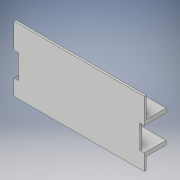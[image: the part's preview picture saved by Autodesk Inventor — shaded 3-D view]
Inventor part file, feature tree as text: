
AUTODESK INVENTOR PART (.ipt)
format: ipt  version: 2019 (Build 230136000, 136)  size: 131,584 bytes
history: native  units: in
note: dims shown in document units (in); Inventor stores cm internally (conversion verified against a paired STEP export)
features: sketch x4, extrude x3
ambient origin geometry x8: Origin, YZ Plane, XZ Plane, XY Plane, X Axis, Y Axis, Z Axis, Center Point
bodies: Solid1 (feature_tree)
feature tree (7):
  extrude  "Extrusion1"  Depth=9.8425in
  sketch  "Sketch2"  dims[d2=0.315in d3=0.0in d4=0.315in d5=0.0in]
  extrude  "Extrusion2"  Depth=0.315in TaperAngle=0.0deg
  extrude  "Extrusion3"  [1 undecoded]
  sketch  "Sketch1"  dims[d0=19.685in d1=9.8425in]
  sketch  "Sketch3"  dims[d6=3.0in d7=0.0in]
  sketch  "Sketch4"
note: 1 required parameter value undecoded (feature->parameter linkage not recoverable at this tier; creation-order binding heuristic only, values carry confidence <= 0.55)
